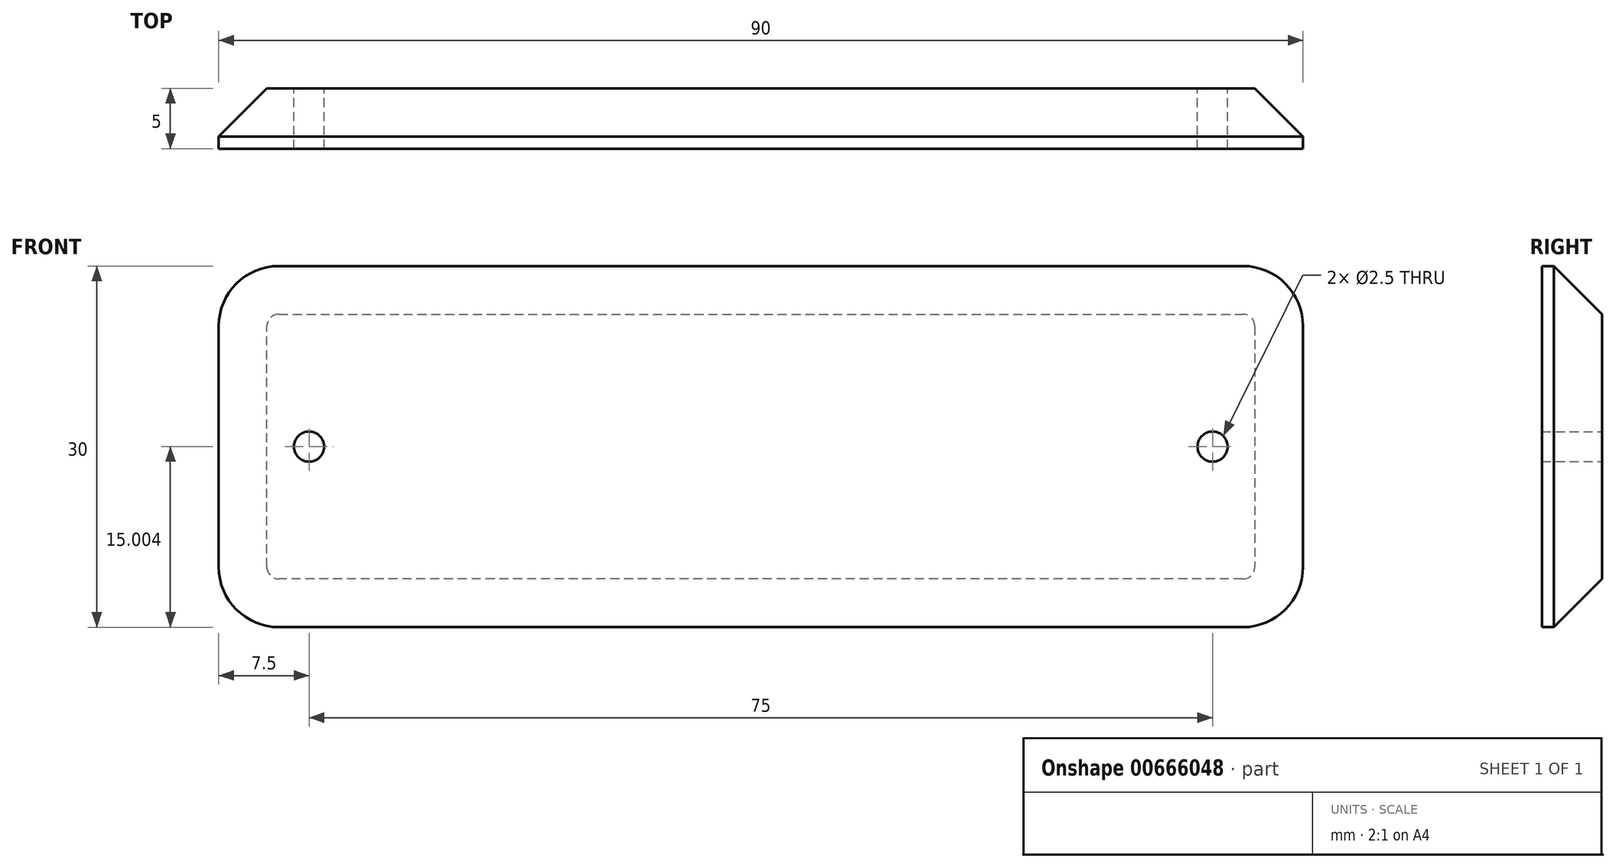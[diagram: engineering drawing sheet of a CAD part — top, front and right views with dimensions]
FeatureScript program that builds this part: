
annotation { "Feature Type Name" : "Feature", "Feature Type Description" : "" }
export const myFeature = defineFeature(function(context is Context, id is Id, definition is map)
    precondition{}
    {
        {
            var Q0;
            Q0=qCreatedBy(makeId("Front.planeOp"),FACE);
            var sketch = newSketch(context, id + "F0", { "sketchPlane" : qUnion([Q0])});
            skLineSegment(sketch, "E0.bottom", {"start": v(-40, 27.08) * mm, "end": v(40, 27.08) * mm});
            skLineSegment(sketch, "E0.top", {"start": v(-40, -2.92) * mm, "end": v(40, -2.92) * mm});
            skLineSegment(sketch, "E0.left", {"start": v(-45, 22.08) * mm, "end": v(-45, 2.08) * mm});
            skLineSegment(sketch, "E0.right", {"start": v(45, 22.08) * mm, "end": v(45, 2.08) * mm});
            skPoint(sketch, "E1.visualSharp", {"position": v(-45, 27.08) * mm});
            skArc(sketch, "E1.filletArc", {"start": v(-40, 27.08) * mm, "mid": v(-43.54, 25.62) * mm, "end": v(-45, 22.08) * mm});
            skPoint(sketch, "E2.visualSharp", {"position": v(-45, -2.92) * mm});
            skArc(sketch, "E2.filletArc", {"start": v(-45, 2.08) * mm, "mid": v(-43.54, -1.45) * mm, "end": v(-40, -2.92) * mm});
            skPoint(sketch, "E3.visualSharp", {"position": v(45, -2.92) * mm});
            skArc(sketch, "E3.filletArc", {"start": v(40, -2.92) * mm, "mid": v(43.54, -1.45) * mm, "end": v(45, 2.08) * mm});
            skPoint(sketch, "E4.visualSharp", {"position": v(45, 27.08) * mm});
            skArc(sketch, "E4.filletArc", {"start": v(45, 22.08) * mm, "mid": v(43.54, 25.62) * mm, "end": v(40, 27.08) * mm});
            skPoint(sketch, "E5", {"position": v(-37.5, 12.08) * mm});
            skPoint(sketch, "E6", {"position": v(37.5, 12.08) * mm});
            skLineSegment(sketch, "E7", {"start": v(45, 12.08) * mm, "end": v(37.5, 12.08) * mm});
            skLineSegment(sketch, "E8", {"start": v(-37.5, 12.08) * mm, "end": v(37.5, 12.08) * mm});
            skLineSegment(sketch, "E9", {"start": v(-37.5, 12.08) * mm, "end": v(-45, 12.08) * mm});
            skSolve(sketch);
        }
        {
            var Q0;
            Q0=makeQuery(id+"F0.imprint","IMPRINT",FACE,{"disambiguationData":[TD([[makeQuery(id+"F0.imprint","IMPRINT",EDGE,{"derivedFrom":sQuery(id+"F0.wireOp",EDGE,"E0.bottom")}),-1.0]])]});
            var Q1;
            Q1=makeQuery(id+"F0.imprint","IMPRINT",FACE,{"disambiguationData":[TD([[makeQuery(id+"F0.imprint","IMPRINT",EDGE,{"derivedFrom":sQuery(id+"F0.wireOp",EDGE,"E0.top")}),1.0]])]});
            extrude(context, id + "F1", {"entities" : qUnion([Q0, Q1]), "depth" : 5 * mm, "offsetDistance" : 25 * mm});
        }
        {
            var Q0;
            Q0=sQuery(id+"F0.wireOp",VERTEX,"E5");
            var Q1;
            Q1=sQuery(id+"F0.wireOp",VERTEX,"E6");
            var Q2;
            Q2=makeQuery(id+"F1.opExtrude","SWEPT_BODY",BODY,{"disambiguationData":[OSD([sQuery(id+"F0.wireOp",EDGE,"E0.bottom"),sQuery(id+"F0.wireOp",EDGE,"E0.top"),sQuery(id+"F0.wireOp",EDGE,"E0.left"),sQuery(id+"F0.wireOp",EDGE,"E0.right"),sQuery(id+"F0.wireOp",EDGE,"E1.filletArc"),sQuery(id+"F0.wireOp",EDGE,"E2.filletArc"),sQuery(id+"F0.wireOp",EDGE,"E3.filletArc"),sQuery(id+"F0.wireOp",EDGE,"E4.filletArc")])]});
            hole(context, id + "F2", {"style" : HoleStyle.SIMPLE, "endStyle" : HoleEndStyle.BLIND, "oppositeDirection" : true, "holeDiameter" : 2.5 * mm, "majorDiameter" : 5 * mm, "holeDepth" : 15 * mm, "isTappedThrough" : true, "tappedDepth" : 7 * mm, "tapClearance" : 3, "startFromSketch" : true, "locations" : qUnion([Q0, Q1]), "scope" : qUnion([Q2])});
        }
        {
            var Q0;
            Q0=makeQuery(id+"F1.opExtrude","CAP_EDGE",EDGE,{"disambiguationData":[OSD([sQuery(id+"F0.wireOp",EDGE,"E0.top")])],"isStart":true});
            chamfer(context, id + "F3", {"entities" : qUnion([Q0]), "width" : 4 * mm, "tangentPropagation" : true});
        }
    });
